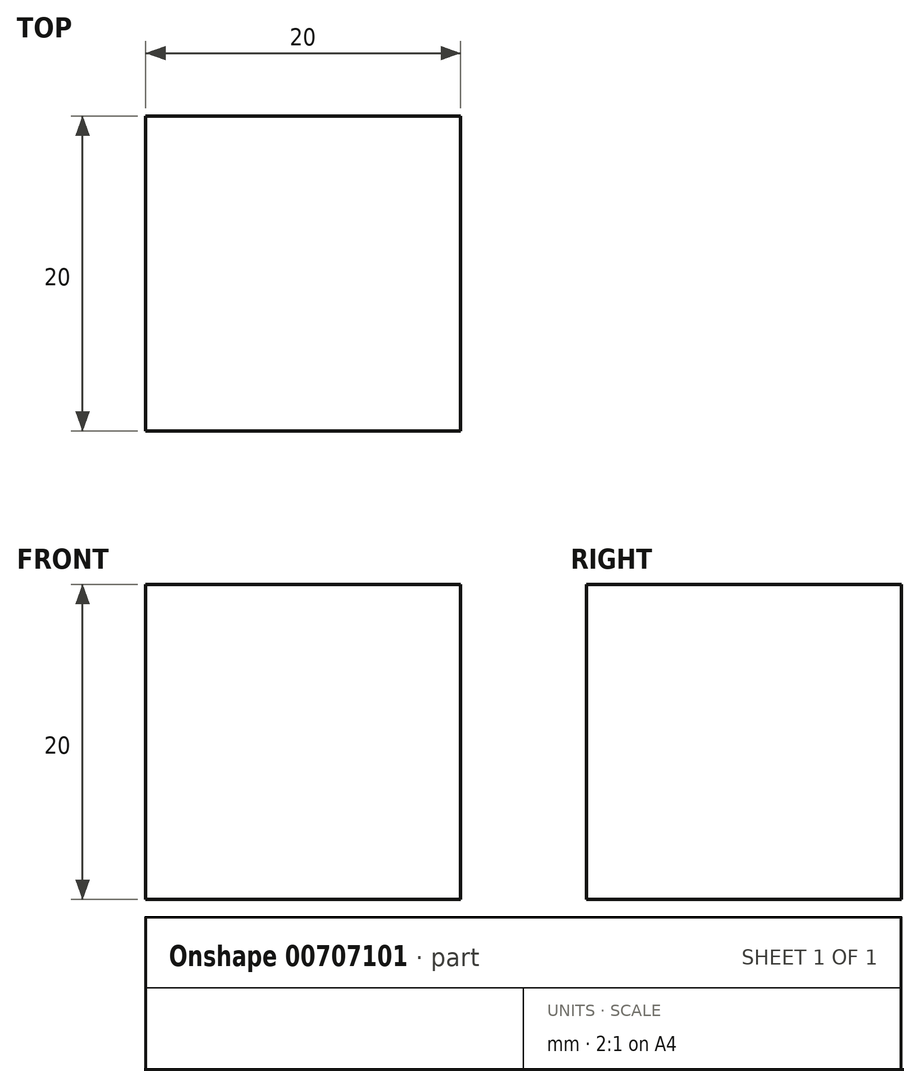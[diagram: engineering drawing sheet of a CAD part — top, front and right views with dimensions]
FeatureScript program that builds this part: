
annotation { "Feature Type Name" : "Feature", "Feature Type Description" : "" }
export const myFeature = defineFeature(function(context is Context, id is Id, definition is map)
    precondition{}
    {
        {
            var Q0;
            Q0=qCreatedBy(makeId("Front.planeOp"),FACE);
            var sketch = newSketch(context, id + "F0", { "sketchPlane" : qUnion([Q0])});
            skLineSegment(sketch, "E0.bottom", {"start": v(0, 0) * mm, "end": v(-20, 0) * mm});
            skLineSegment(sketch, "E0.top", {"start": v(0, 20) * mm, "end": v(-20, 20) * mm});
            skLineSegment(sketch, "E0.left", {"start": v(0, 0) * mm, "end": v(0, 20) * mm});
            skLineSegment(sketch, "E0.right", {"start": v(-20, 0) * mm, "end": v(-20, 20) * mm});
            skSolve(sketch);
        }
        {
            var Q0;
            Q0 = qSketchRegion(id + "F0", true);
            var Q1;
            Q1=makeQuery(id+"F0.imprint","IMPRINT",FACE,{"disambiguationData":[TD([[makeQuery(id+"F0.imprint","IMPRINT",EDGE,{"derivedFrom":sQuery(id+"F0.wireOp",EDGE,"E0.bottom")}),-1.0]])]});
            extrude(context, id + "F1", {"entities" : qUnion([Q0, Q1]), "depth" : 20 * mm, "offsetDistance" : 25 * mm});
        }
    });
